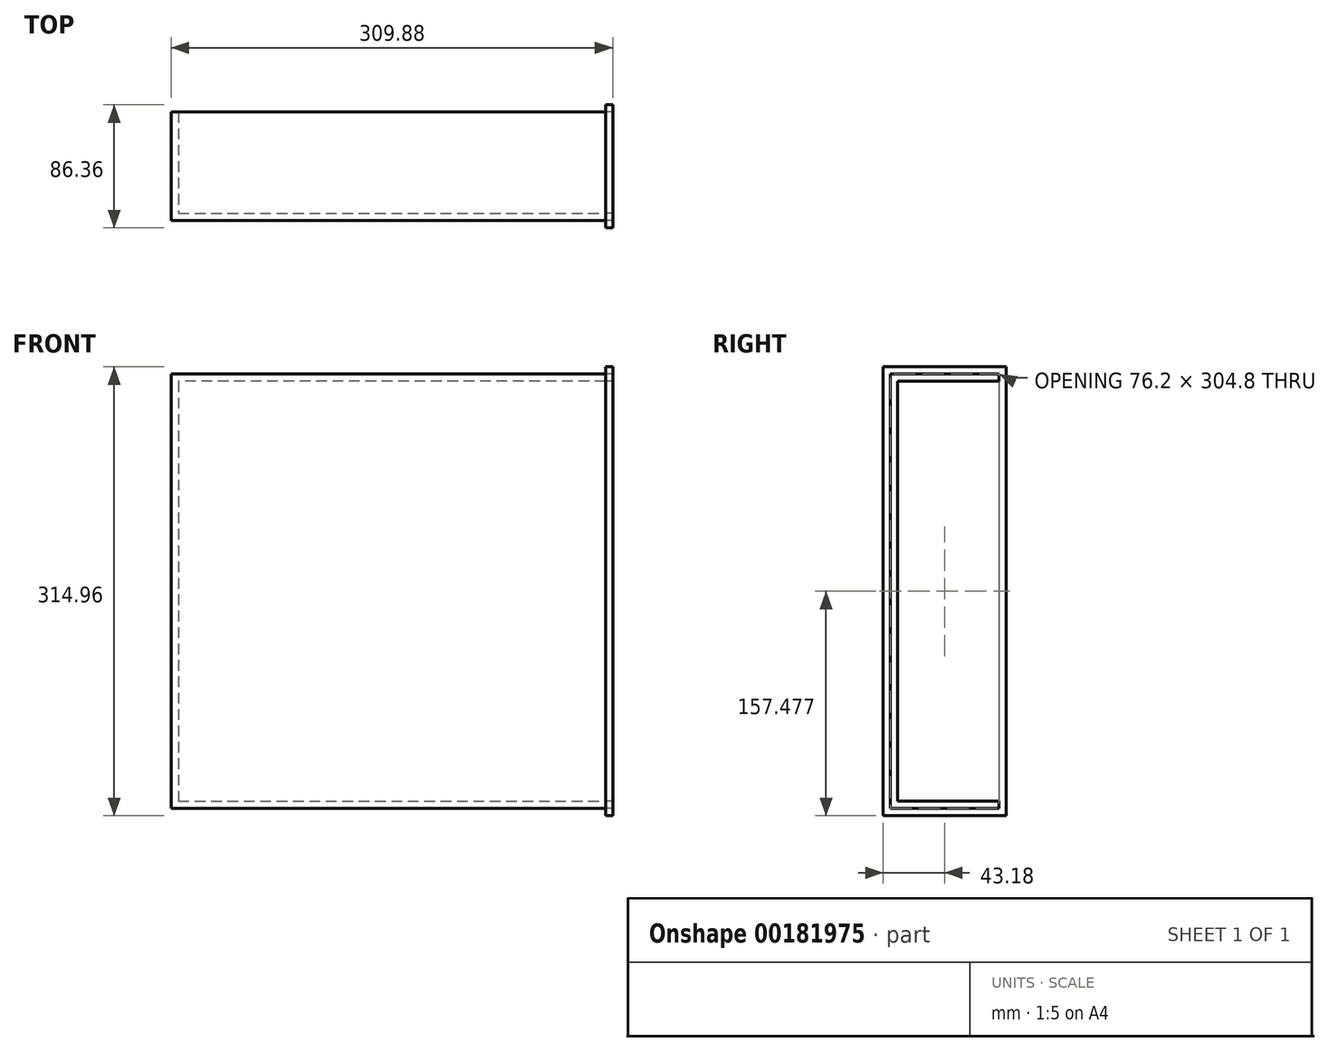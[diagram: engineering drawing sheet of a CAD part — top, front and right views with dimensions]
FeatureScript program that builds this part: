
annotation { "Feature Type Name" : "Feature", "Feature Type Description" : "" }
export const myFeature = defineFeature(function(context is Context, id is Id, definition is map)
    precondition{}
    {
        {
            var Q0;
            Q0=qCreatedBy(makeId("Front.planeOp"),FACE);
            var sketch = newSketch(context, id + "F0", { "sketchPlane" : qUnion([Q0])});
            skLineSegment(sketch, "E0", {"start": v(-267.38, 153.23) * mm, "end": v(37.42, 153.23) * mm});
            skLineSegment(sketch, "E1", {"start": v(-267.38, 153.23) * mm, "end": v(-267.38, -151.57) * mm});
            skLineSegment(sketch, "E2", {"start": v(37.42, 153.23) * mm, "end": v(37.42, 148.15) * mm});
            skLineSegment(sketch, "E3", {"start": v(37.42, 148.15) * mm, "end": v(-262.3, 148.15) * mm});
            skLineSegment(sketch, "E4", {"start": v(-262.3, 148.15) * mm, "end": v(-262.3, -146.5) * mm});
            skLineSegment(sketch, "E5", {"start": v(-267.38, -151.57) * mm, "end": v(37.42, -151.57) * mm});
            skLineSegment(sketch, "E6", {"start": v(-262.3, -146.5) * mm, "end": v(37.42, -146.5) * mm});
            skLineSegment(sketch, "E7", {"start": v(37.42, -146.5) * mm, "end": v(37.42, 153.23) * mm});
            skLineSegment(sketch, "E8", {"start": v(37.42, -146.5) * mm, "end": v(37.42, -151.57) * mm});
            skSolve(sketch);
        }
        {
            var Q0;
            Q0 = qSketchRegion(id + "F0", true);
            extrude(context, id + "F1", {"entities" : qUnion([Q0]), "depth" : 5.08 * mm});
        }
        {
            var Q0;
            {var subQ1=sQuery(id+"F0.wireOp",EDGE,"E0");Q0=makeQuery(id+"F0.imprint","IMPRINT",FACE,{"disambiguationData":[TD([[makeQuery(id+"F0.imprint","IMPRINT",EDGE,{"derivedFrom":subQ1}),-1.0]])]});}
            extrude(context, id + "F2", {"entities" : qUnion([Q0]), "operationType" : NewBodyOperationType.ADD, "oppositeDirection" : true, "depth" : 71.12 * mm});
        }
        {
            var Q0;
            {var subQ0=sQuery(id+"F0.wireOp",EDGE,"E8");var subQ1=sQuery(id+"F0.wireOp",EDGE,"E7");Q0=makeQuery(id+"F2.boolean.opBoolean","MERGE",FACE,{"derivedFrom":[makeQuery(id+"F1.opExtrude","SWEPT_FACE",FACE,{"disambiguationData":[OSD([subQ1,subQ0])]}),makeQuery(id+"F2.opExtrude","SWEPT_FACE",FACE,{"disambiguationData":[OSD([subQ1])]}),makeQuery(id+"F2.opExtrude","SWEPT_FACE",FACE,{"disambiguationData":[OSD([subQ0])]})]});}
            var sketch = newSketch(context, id + "F3", { "sketchPlane" : qUnion([Q0])});
            skLineSegment(sketch, "E9", {"start": v(76.2, 158.3) * mm, "end": v(-10.16, 158.3) * mm});
            skLineSegment(sketch, "E10", {"start": v(-10.16, 158.3) * mm, "end": v(-10.16, -156.65) * mm});
            skLineSegment(sketch, "E11", {"start": v(-10.16, -156.65) * mm, "end": v(76.2, -156.65) * mm});
            skLineSegment(sketch, "E12", {"start": v(76.2, 158.3) * mm, "end": v(76.2, -156.65) * mm});
            skSolve(sketch);
        }
        {
            var Q0;
            Q0=makeQuery(id+"F3.imprint","IMPRINT",FACE,{"disambiguationData":[TD([[makeQuery(id+"F3.imprint","IMPRINT",EDGE,{"derivedFrom":sQuery(id+"F3.wireOp",EDGE,"E9")}),1.0]])]});
            var Q1;
            {var subQ0=sQuery(id+"F0.wireOp",EDGE,"E7");Q1=makeQuery(id+"F3.imprint","IMPRINT",FACE,{"disambiguationData":[TD([[makeQuery(id+"F3.imprint","IMPRINT",EDGE,{"derivedFrom":makeQuery(id+"F2.opExtrude","CAP_EDGE",EDGE,{"disambiguationData":[OSD([subQ0])],"isStart":false})}),1.0]])]});}
            extrude(context, id + "F4", {"entities" : qUnion([Q0, Q1]), "depth" : 5.08 * mm});
        }
    });
